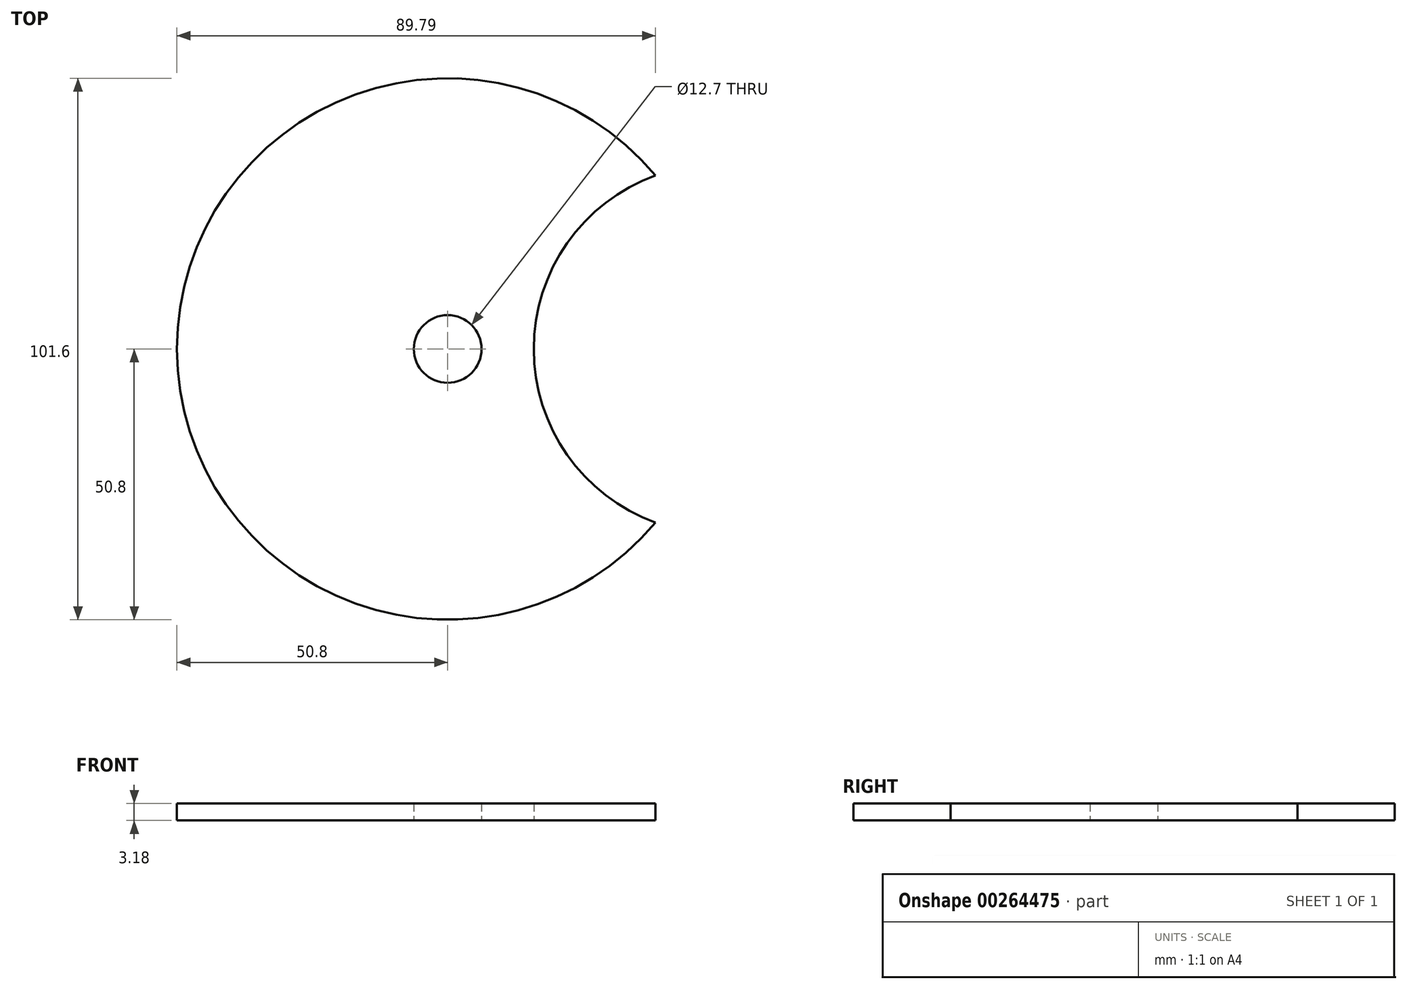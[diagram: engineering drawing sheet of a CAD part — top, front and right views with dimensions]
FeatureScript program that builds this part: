
annotation { "Feature Type Name" : "Feature", "Feature Type Description" : "" }
export const myFeature = defineFeature(function(context is Context, id is Id, definition is map)
    precondition{}
    {
        {
            var Q0;
            Q0=qCreatedBy(makeId("Top.planeOp"),FACE);
            var sketch = newSketch(context, id + "F0", { "sketchPlane" : qUnion([Q0])});
            skArc(sketch, "E0", {"start": v(38.99, 32.57) * mm, "mid": v(-50.8, 0) * mm, "end": v(38.99, -32.57) * mm});
            skCircle(sketch, "E1", {"center": v(0, 0) * mm, "radius": 6.35 * mm});
            skArc(sketch, "E2", {"start": v(38.99, -32.57) * mm, "mid": v(16.15, 0) * mm, "end": v(38.99, 32.57) * mm});
            skSolve(sketch);
        }
        {
            var Q0;
            Q0=makeQuery(id+"F0.imprint","IMPRINT",FACE,{"disambiguationData":[TD([[makeQuery(id+"F0.imprint","IMPRINT",EDGE,{"derivedFrom":sQuery(id+"F0.wireOp",EDGE,"E0")}),1.0]])]});
            extrude(context, id + "F1", {"entities" : qUnion([Q0]), "depth" : 3.17 * mm});
        }
    });
